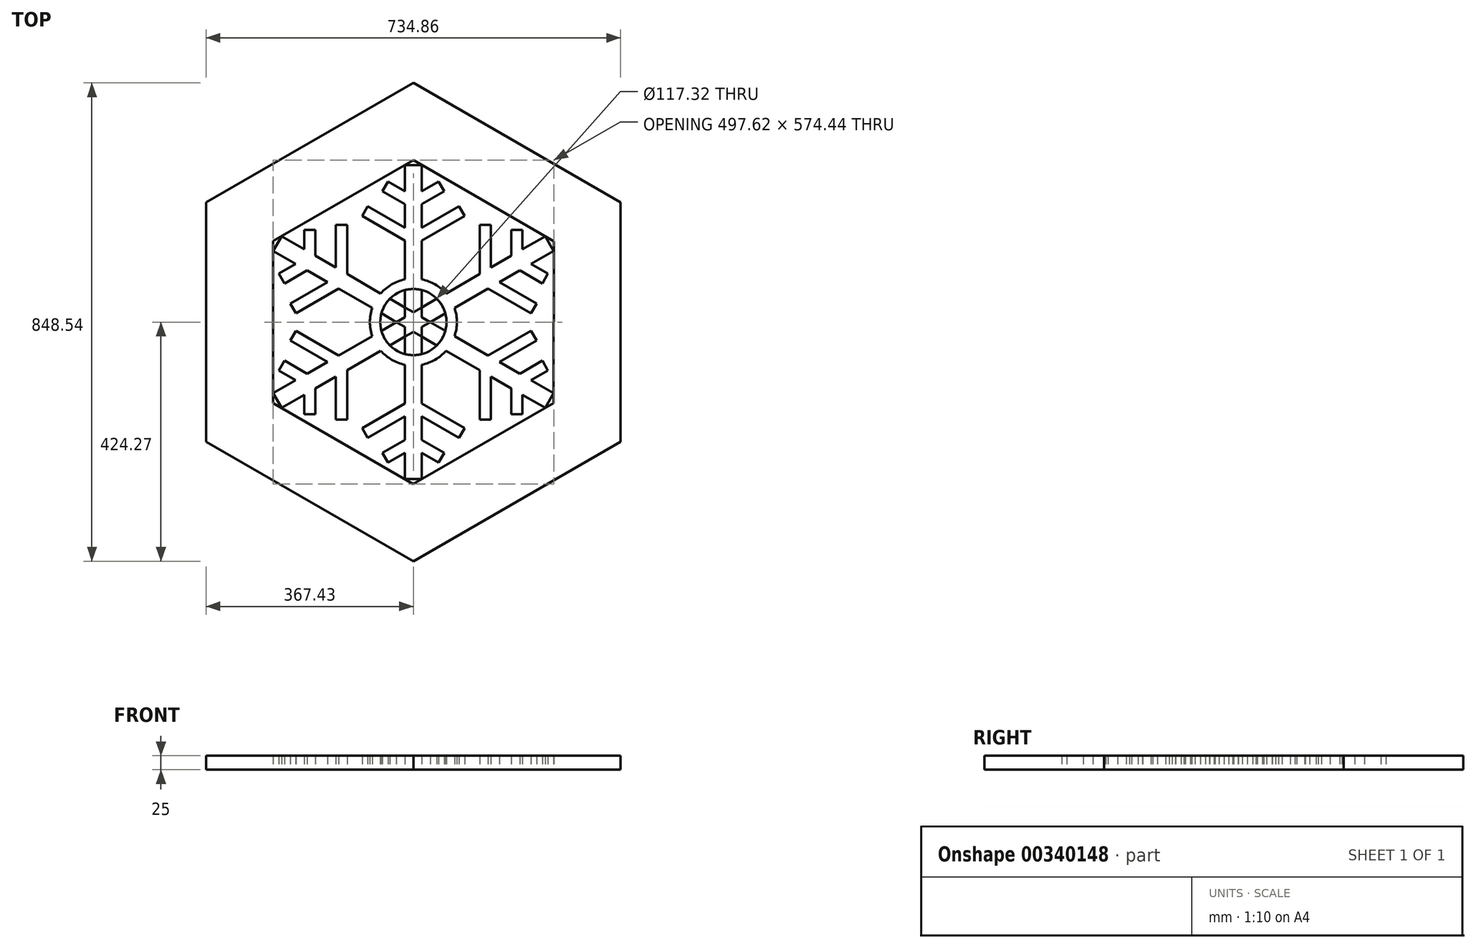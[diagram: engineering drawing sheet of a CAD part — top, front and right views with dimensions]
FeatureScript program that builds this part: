
annotation { "Feature Type Name" : "Feature", "Feature Type Description" : "" }
export const myFeature = defineFeature(function(context is Context, id is Id, definition is map)
    precondition{}
    {
        {
            var Q0;
            Q0=qCreatedBy(makeId("Top.planeOp"),FACE);
            var sketch = newSketch(context, id + "F0", { "sketchPlane" : qUnion([Q0])});
            skLineSegment(sketch, "E0", {"start": v(0, 439.87) * mm, "end": v(0, -254.88) * mm, "construction": true});
            skLineSegment(sketch, "E1", {"start": v(0, 278.5) * mm, "end": v(-15, 278.5) * mm});
            skLineSegment(sketch, "E2", {"start": v(-15, 278.5) * mm, "end": v(-15, 232.17) * mm});
            skLineSegment(sketch, "E3", {"start": v(-15, 232.17) * mm, "end": v(-45, 249.5) * mm});
            skLineSegment(sketch, "E4", {"start": v(-45, 249.5) * mm, "end": v(-55, 232.17) * mm});
            skLineSegment(sketch, "E5", {"start": v(-55, 232.17) * mm, "end": v(-15, 209.08) * mm});
            skLineSegment(sketch, "E6", {"start": v(-45, 249.5) * mm, "end": v(-55, 232.17) * mm, "construction": true});
            skLineSegment(sketch, "E7", {"start": v(-40.34, 275.63) * mm, "end": v(-118.1, 140.94) * mm, "construction": true});
            skLineSegment(sketch, "E8", {"start": v(-15, 209.08) * mm, "end": v(-15, 167.41) * mm});
            skLineSegment(sketch, "E9", {"start": v(-15, 167.41) * mm, "end": v(-80.86, 205.44) * mm});
            skLineSegment(sketch, "E10", {"start": v(-80.86, 205.44) * mm, "end": v(-90.86, 188.12) * mm});
            skLineSegment(sketch, "E11", {"start": v(-90.86, 188.12) * mm, "end": v(-15, 144.32) * mm});
            skLineSegment(sketch, "E12", {"start": v(-15, 144.32) * mm, "end": v(-15, 0) * mm});
            skLineSegment(sketch, "E13", {"start": v(-15, 0) * mm, "end": v(0, 0) * mm});
            skLineSegment(sketch, "E14.MirrorCS", {"start": v(0, 278.5) * mm, "end": v(15, 278.5) * mm});
            skLineSegment(sketch, "E15.MirrorCS", {"start": v(15, 278.5) * mm, "end": v(15, 232.17) * mm});
            skLineSegment(sketch, "E16.MirrorCS", {"start": v(15, 232.17) * mm, "end": v(45, 249.5) * mm});
            skLineSegment(sketch, "E17.MirrorCS", {"start": v(45, 249.5) * mm, "end": v(55, 232.17) * mm});
            skLineSegment(sketch, "E18.MirrorCS", {"start": v(55, 232.17) * mm, "end": v(15, 209.08) * mm});
            skLineSegment(sketch, "E19.MirrorCS", {"start": v(15, 167.41) * mm, "end": v(80.86, 205.44) * mm});
            skLineSegment(sketch, "E20.MirrorCS", {"start": v(15, 209.08) * mm, "end": v(15, 167.41) * mm});
            skLineSegment(sketch, "E21.MirrorCS", {"start": v(90.86, 188.12) * mm, "end": v(15, 144.32) * mm});
            skLineSegment(sketch, "E22.MirrorCS", {"start": v(80.86, 205.44) * mm, "end": v(90.86, 188.12) * mm});
            skLineSegment(sketch, "E23.MirrorCS", {"start": v(15, 144.32) * mm, "end": v(15, 0) * mm});
            skLineSegment(sketch, "E24.MirrorCS", {"start": v(15, 0) * mm, "end": v(0, 0) * mm});
            skLineSegment(sketch, "E25.1.0", {"start": v(-193.57, 129.08) * mm, "end": v(-193.57, 163.72) * mm});
            skLineSegment(sketch, "E25.1.1", {"start": v(-238.57, 85.77) * mm, "end": v(-228.57, 68.45) * mm, "construction": true});
            skLineSegment(sketch, "E25.1.2", {"start": v(-228.57, 68.45) * mm, "end": v(-188.57, 91.55) * mm});
            skLineSegment(sketch, "E25.1.3", {"start": v(-173.57, 163.72) * mm, "end": v(-173.57, 117.53) * mm});
            skLineSegment(sketch, "E25.1.4", {"start": v(-188.57, 91.55) * mm, "end": v(-152.49, 70.72) * mm});
            skLineSegment(sketch, "E25.1.5", {"start": v(-258.87, 102.88) * mm, "end": v(-181.1, -31.81) * mm, "construction": true});
            skLineSegment(sketch, "E25.1.6", {"start": v(-173.57, 117.53) * mm, "end": v(-137.49, 96.7) * mm});
            skLineSegment(sketch, "E25.1.7", {"start": v(-208.57, 103.1) * mm, "end": v(-238.57, 85.77) * mm});
            skLineSegment(sketch, "E25.1.8", {"start": v(-248.68, 126.26) * mm, "end": v(-208.57, 103.1) * mm});
            skLineSegment(sketch, "E25.1.9", {"start": v(-152.49, 70.72) * mm, "end": v(-218.35, 32.7) * mm});
            skLineSegment(sketch, "E25.1.10", {"start": v(-208.35, 15.37) * mm, "end": v(-132.49, 59.17) * mm});
            skLineSegment(sketch, "E25.1.11", {"start": v(-117.49, 85.15) * mm, "end": v(7.5, 13) * mm});
            skLineSegment(sketch, "E25.1.12", {"start": v(-137.49, 172.75) * mm, "end": v(-117.49, 172.75) * mm});
            skLineSegment(sketch, "E25.1.13", {"start": v(-117.49, 172.75) * mm, "end": v(-117.49, 85.15) * mm});
            skLineSegment(sketch, "E25.1.14", {"start": v(-132.49, 59.17) * mm, "end": v(-7.5, -13) * mm});
            skLineSegment(sketch, "E25.1.15", {"start": v(-137.49, 96.7) * mm, "end": v(-137.49, 172.75) * mm});
            skLineSegment(sketch, "E25.1.16", {"start": v(-233.68, 152.24) * mm, "end": v(-193.57, 129.08) * mm});
            skLineSegment(sketch, "E25.1.17", {"start": v(-193.57, 163.72) * mm, "end": v(-173.57, 163.72) * mm});
            skLineSegment(sketch, "E25.1.18", {"start": v(-238.57, 85.77) * mm, "end": v(-228.57, 68.45) * mm});
            skLineSegment(sketch, "E25.1.19", {"start": v(-218.35, 32.7) * mm, "end": v(-208.35, 15.37) * mm});
            skLineSegment(sketch, "E25.1.20", {"start": v(-241.18, 139.25) * mm, "end": v(-233.68, 152.24) * mm});
            skLineSegment(sketch, "E25.1.21", {"start": v(7.5, 13) * mm, "end": v(0, 0) * mm});
            skLineSegment(sketch, "E25.1.22", {"start": v(-7.5, -13) * mm, "end": v(0, 0) * mm});
            skLineSegment(sketch, "E25.1.23", {"start": v(-241.18, 139.25) * mm, "end": v(-248.68, 126.26) * mm});
            skLineSegment(sketch, "E25.2.0", {"start": v(-208.57, -103.1) * mm, "end": v(-238.57, -85.77) * mm});
            skLineSegment(sketch, "E25.2.1", {"start": v(-193.57, -163.72) * mm, "end": v(-173.57, -163.72) * mm, "construction": true});
            skLineSegment(sketch, "E25.2.2", {"start": v(-173.57, -163.72) * mm, "end": v(-173.57, -117.53) * mm});
            skLineSegment(sketch, "E25.2.3", {"start": v(-228.57, -68.45) * mm, "end": v(-188.57, -91.55) * mm});
            skLineSegment(sketch, "E25.2.4", {"start": v(-173.57, -117.53) * mm, "end": v(-137.49, -96.7) * mm});
            skLineSegment(sketch, "E25.2.5", {"start": v(-218.53, -172.75) * mm, "end": v(-63, -172.75) * mm, "construction": true});
            skLineSegment(sketch, "E25.2.6", {"start": v(-188.57, -91.55) * mm, "end": v(-152.49, -70.72) * mm});
            skLineSegment(sketch, "E25.2.7", {"start": v(-193.57, -129.08) * mm, "end": v(-193.57, -163.72) * mm});
            skLineSegment(sketch, "E25.2.8", {"start": v(-233.68, -152.24) * mm, "end": v(-193.57, -129.08) * mm});
            skLineSegment(sketch, "E25.2.9", {"start": v(-137.49, -96.7) * mm, "end": v(-137.49, -172.75) * mm});
            skLineSegment(sketch, "E25.2.10", {"start": v(-117.49, -172.75) * mm, "end": v(-117.49, -85.15) * mm});
            skLineSegment(sketch, "E25.2.11", {"start": v(-132.49, -59.17) * mm, "end": v(-7.5, 13) * mm});
            skLineSegment(sketch, "E25.2.12", {"start": v(-218.35, -32.7) * mm, "end": v(-208.35, -15.37) * mm});
            skLineSegment(sketch, "E25.2.13", {"start": v(-208.35, -15.37) * mm, "end": v(-132.49, -59.17) * mm});
            skLineSegment(sketch, "E25.2.14", {"start": v(-117.49, -85.15) * mm, "end": v(7.5, -13) * mm});
            skLineSegment(sketch, "E25.2.15", {"start": v(-152.49, -70.72) * mm, "end": v(-218.35, -32.7) * mm});
            skLineSegment(sketch, "E25.2.16", {"start": v(-248.68, -126.26) * mm, "end": v(-208.57, -103.1) * mm});
            skLineSegment(sketch, "E25.2.17", {"start": v(-238.57, -85.77) * mm, "end": v(-228.57, -68.45) * mm});
            skLineSegment(sketch, "E25.2.18", {"start": v(-193.57, -163.72) * mm, "end": v(-173.57, -163.72) * mm});
            skLineSegment(sketch, "E25.2.19", {"start": v(-137.49, -172.75) * mm, "end": v(-117.49, -172.75) * mm});
            skLineSegment(sketch, "E25.2.20", {"start": v(-241.18, -139.25) * mm, "end": v(-248.68, -126.26) * mm});
            skLineSegment(sketch, "E25.2.21", {"start": v(-7.5, 13) * mm, "end": v(0, 0) * mm});
            skLineSegment(sketch, "E25.2.22", {"start": v(7.5, -13) * mm, "end": v(0, 0) * mm});
            skLineSegment(sketch, "E25.2.23", {"start": v(-241.18, -139.25) * mm, "end": v(-233.68, -152.24) * mm});
            skLineSegment(sketch, "E25.3.0", {"start": v(-15, -232.17) * mm, "end": v(-45, -249.5) * mm});
            skLineSegment(sketch, "E25.3.1", {"start": v(45, -249.5) * mm, "end": v(55, -232.17) * mm, "construction": true});
            skLineSegment(sketch, "E25.3.2", {"start": v(55, -232.17) * mm, "end": v(15, -209.08) * mm});
            skLineSegment(sketch, "E25.3.3", {"start": v(-55, -232.17) * mm, "end": v(-15, -209.08) * mm});
            skLineSegment(sketch, "E25.3.4", {"start": v(15, -209.08) * mm, "end": v(15, -167.41) * mm});
            skLineSegment(sketch, "E25.3.5", {"start": v(40.34, -275.63) * mm, "end": v(118.1, -140.94) * mm, "construction": true});
            skLineSegment(sketch, "E25.3.6", {"start": v(-15, -209.08) * mm, "end": v(-15, -167.41) * mm});
            skLineSegment(sketch, "E25.3.7", {"start": v(15, -232.17) * mm, "end": v(45, -249.5) * mm});
            skLineSegment(sketch, "E25.3.8", {"start": v(15, -278.5) * mm, "end": v(15, -232.17) * mm});
            skLineSegment(sketch, "E25.3.9", {"start": v(15, -167.41) * mm, "end": v(80.86, -205.44) * mm});
            skLineSegment(sketch, "E25.3.10", {"start": v(90.86, -188.12) * mm, "end": v(15, -144.32) * mm});
            skLineSegment(sketch, "E25.3.11", {"start": v(-15, -144.32) * mm, "end": v(-15, 0) * mm});
            skLineSegment(sketch, "E25.3.12", {"start": v(-80.86, -205.44) * mm, "end": v(-90.86, -188.12) * mm});
            skLineSegment(sketch, "E25.3.13", {"start": v(-90.86, -188.12) * mm, "end": v(-15, -144.32) * mm});
            skLineSegment(sketch, "E25.3.14", {"start": v(15, -144.32) * mm, "end": v(15, 0) * mm});
            skLineSegment(sketch, "E25.3.15", {"start": v(-15, -167.41) * mm, "end": v(-80.86, -205.44) * mm});
            skLineSegment(sketch, "E25.3.16", {"start": v(-15, -278.5) * mm, "end": v(-15, -232.17) * mm});
            skLineSegment(sketch, "E25.3.17", {"start": v(-45, -249.5) * mm, "end": v(-55, -232.17) * mm});
            skLineSegment(sketch, "E25.3.18", {"start": v(45, -249.5) * mm, "end": v(55, -232.17) * mm});
            skLineSegment(sketch, "E25.3.19", {"start": v(80.86, -205.44) * mm, "end": v(90.86, -188.12) * mm});
            skLineSegment(sketch, "E25.3.20", {"start": v(0, -278.5) * mm, "end": v(-15, -278.5) * mm});
            skLineSegment(sketch, "E25.3.23", {"start": v(0, -278.5) * mm, "end": v(15, -278.5) * mm});
            skLineSegment(sketch, "E25.4.0", {"start": v(193.57, -129.08) * mm, "end": v(193.57, -163.72) * mm});
            skLineSegment(sketch, "E25.4.1", {"start": v(238.57, -85.77) * mm, "end": v(228.57, -68.45) * mm, "construction": true});
            skLineSegment(sketch, "E25.4.2", {"start": v(228.57, -68.45) * mm, "end": v(188.57, -91.55) * mm});
            skLineSegment(sketch, "E25.4.3", {"start": v(173.57, -163.72) * mm, "end": v(173.57, -117.53) * mm});
            skLineSegment(sketch, "E25.4.4", {"start": v(188.57, -91.55) * mm, "end": v(152.49, -70.72) * mm});
            skLineSegment(sketch, "E25.4.5", {"start": v(258.87, -102.88) * mm, "end": v(181.1, 31.81) * mm, "construction": true});
            skLineSegment(sketch, "E25.4.6", {"start": v(173.57, -117.53) * mm, "end": v(137.49, -96.7) * mm});
            skLineSegment(sketch, "E25.4.7", {"start": v(208.57, -103.1) * mm, "end": v(238.57, -85.77) * mm});
            skLineSegment(sketch, "E25.4.8", {"start": v(248.68, -126.26) * mm, "end": v(208.57, -103.1) * mm});
            skLineSegment(sketch, "E25.4.9", {"start": v(152.49, -70.72) * mm, "end": v(218.35, -32.7) * mm});
            skLineSegment(sketch, "E25.4.10", {"start": v(208.35, -15.37) * mm, "end": v(132.49, -59.17) * mm});
            skLineSegment(sketch, "E25.4.11", {"start": v(117.49, -85.15) * mm, "end": v(-7.5, -13) * mm});
            skLineSegment(sketch, "E25.4.12", {"start": v(137.49, -172.75) * mm, "end": v(117.49, -172.75) * mm});
            skLineSegment(sketch, "E25.4.13", {"start": v(117.49, -172.75) * mm, "end": v(117.49, -85.15) * mm});
            skLineSegment(sketch, "E25.4.14", {"start": v(132.49, -59.17) * mm, "end": v(7.5, 13) * mm});
            skLineSegment(sketch, "E25.4.15", {"start": v(137.49, -96.7) * mm, "end": v(137.49, -172.75) * mm});
            skLineSegment(sketch, "E25.4.16", {"start": v(233.68, -152.24) * mm, "end": v(193.57, -129.08) * mm});
            skLineSegment(sketch, "E25.4.17", {"start": v(193.57, -163.72) * mm, "end": v(173.57, -163.72) * mm});
            skLineSegment(sketch, "E25.4.18", {"start": v(238.57, -85.77) * mm, "end": v(228.57, -68.45) * mm});
            skLineSegment(sketch, "E25.4.19", {"start": v(218.35, -32.7) * mm, "end": v(208.35, -15.37) * mm});
            skLineSegment(sketch, "E25.4.20", {"start": v(241.18, -139.25) * mm, "end": v(233.68, -152.24) * mm});
            skLineSegment(sketch, "E25.4.21", {"start": v(-7.5, -13) * mm, "end": v(0, 0) * mm});
            skLineSegment(sketch, "E25.4.22", {"start": v(7.5, 13) * mm, "end": v(0, 0) * mm});
            skLineSegment(sketch, "E25.4.23", {"start": v(241.18, -139.25) * mm, "end": v(248.68, -126.26) * mm});
            skLineSegment(sketch, "E25.5.0", {"start": v(208.57, 103.1) * mm, "end": v(238.57, 85.77) * mm});
            skLineSegment(sketch, "E25.5.1", {"start": v(193.57, 163.72) * mm, "end": v(173.57, 163.72) * mm, "construction": true});
            skLineSegment(sketch, "E25.5.2", {"start": v(173.57, 163.72) * mm, "end": v(173.57, 117.53) * mm});
            skLineSegment(sketch, "E25.5.3", {"start": v(228.57, 68.45) * mm, "end": v(188.57, 91.55) * mm});
            skLineSegment(sketch, "E25.5.4", {"start": v(173.57, 117.53) * mm, "end": v(137.49, 96.7) * mm});
            skLineSegment(sketch, "E25.5.5", {"start": v(218.53, 172.75) * mm, "end": v(63, 172.75) * mm, "construction": true});
            skLineSegment(sketch, "E25.5.6", {"start": v(188.57, 91.55) * mm, "end": v(152.49, 70.72) * mm});
            skLineSegment(sketch, "E25.5.7", {"start": v(193.57, 129.08) * mm, "end": v(193.57, 163.72) * mm});
            skLineSegment(sketch, "E25.5.8", {"start": v(233.68, 152.24) * mm, "end": v(193.57, 129.08) * mm});
            skLineSegment(sketch, "E25.5.9", {"start": v(137.49, 96.7) * mm, "end": v(137.49, 172.75) * mm});
            skLineSegment(sketch, "E25.5.10", {"start": v(117.49, 172.75) * mm, "end": v(117.49, 85.15) * mm});
            skLineSegment(sketch, "E25.5.11", {"start": v(132.49, 59.17) * mm, "end": v(7.5, -13) * mm});
            skLineSegment(sketch, "E25.5.12", {"start": v(218.35, 32.7) * mm, "end": v(208.35, 15.37) * mm});
            skLineSegment(sketch, "E25.5.13", {"start": v(208.35, 15.37) * mm, "end": v(132.49, 59.17) * mm});
            skLineSegment(sketch, "E25.5.14", {"start": v(117.49, 85.15) * mm, "end": v(-7.5, 13) * mm});
            skLineSegment(sketch, "E25.5.15", {"start": v(152.49, 70.72) * mm, "end": v(218.35, 32.7) * mm});
            skLineSegment(sketch, "E25.5.16", {"start": v(248.68, 126.26) * mm, "end": v(208.57, 103.1) * mm});
            skLineSegment(sketch, "E25.5.17", {"start": v(238.57, 85.77) * mm, "end": v(228.57, 68.45) * mm});
            skLineSegment(sketch, "E25.5.18", {"start": v(193.57, 163.72) * mm, "end": v(173.57, 163.72) * mm});
            skLineSegment(sketch, "E25.5.19", {"start": v(137.49, 172.75) * mm, "end": v(117.49, 172.75) * mm});
            skLineSegment(sketch, "E25.5.20", {"start": v(241.18, 139.25) * mm, "end": v(248.68, 126.26) * mm});
            skLineSegment(sketch, "E25.5.21", {"start": v(7.5, -13) * mm, "end": v(0, 0) * mm});
            skLineSegment(sketch, "E25.5.22", {"start": v(-7.5, 13) * mm, "end": v(0, 0) * mm});
            skLineSegment(sketch, "E25.5.23", {"start": v(241.18, 139.25) * mm, "end": v(233.68, 152.24) * mm});
            skPoint(sketch, "E25.center", {"position": v(0, 0) * mm});
            skCircle(sketch, "E26", {"center": v(0, 0) * mm, "radius": 77.12 * mm});
            skCircle(sketch, "E27", {"center": v(0, 0) * mm, "radius": 58.66 * mm});
            skCircle(sketch, "E28.cCircle", {"center": v(0, 0) * mm, "radius": 367.43 * mm, "construction": true});
            skLineSegment(sketch, "E28.0", {"start": v(367.43, -212.14) * mm, "end": v(0, -424.27) * mm});
            skLineSegment(sketch, "E28.1", {"start": v(0, -424.27) * mm, "end": v(-367.43, -212.14) * mm});
            skLineSegment(sketch, "E28.2", {"start": v(-367.43, -212.14) * mm, "end": v(-367.43, 212.14) * mm});
            skLineSegment(sketch, "E28.3", {"start": v(-367.43, 212.14) * mm, "end": v(0, 424.27) * mm});
            skLineSegment(sketch, "E28.4", {"start": v(0, 424.27) * mm, "end": v(367.43, 212.14) * mm});
            skLineSegment(sketch, "E28.5", {"start": v(367.43, 212.14) * mm, "end": v(367.43, -212.14) * mm});
            skPoint(sketch, "E28.0.midPoint", {"position": v(183.72, -318.2) * mm});
            skCircle(sketch, "E29.cCircle", {"center": v(0, 0) * mm, "radius": 248.74 * mm, "construction": true});
            skLineSegment(sketch, "E29.0", {"start": v(-248.67, 143.73) * mm, "end": v(0.14, 287.22) * mm});
            skLineSegment(sketch, "E29.1", {"start": v(0.14, 287.22) * mm, "end": v(248.8, 143.5) * mm});
            skLineSegment(sketch, "E29.2", {"start": v(248.8, 143.5) * mm, "end": v(248.67, -143.73) * mm});
            skLineSegment(sketch, "E29.3", {"start": v(248.67, -143.73) * mm, "end": v(-0.14, -287.22) * mm});
            skLineSegment(sketch, "E29.4", {"start": v(-0.14, -287.22) * mm, "end": v(-248.8, -143.5) * mm});
            skLineSegment(sketch, "E29.5", {"start": v(-248.8, -143.5) * mm, "end": v(-248.67, 143.73) * mm});
            skPoint(sketch, "E29.0.midPoint", {"position": v(-124.27, 215.48) * mm});
            skSolve(sketch);
        }
        {
            var Q0;
            Q0=makeQuery(id+"F0.imprint","IMPRINT",FACE,{"disambiguationData":[TD([[makeQuery(id+"F0.imprint","IMPRINT",EDGE,{"derivedFrom":sQuery(id+"F0.wireOp",EDGE,"E28.0")}),-1.0]])]});
            var Q1;
            Q1=makeQuery(id+"F0.imprint","IMPRINT",FACE,{"disambiguationData":[TD([[makeQuery(id+"F0.imprint","IMPRINT",EDGE,{"derivedFrom":sQuery(id+"F0.wireOp",EDGE,"E25.1.0")}),-1.0]])]});
            var Q2;
            Q2=makeQuery(id+"F0.imprint","IMPRINT",FACE,{"disambiguationData":[TD([[makeQuery(id+"F0.imprint","IMPRINT",EDGE,{"derivedFrom":sQuery(id+"F0.wireOp",EDGE,"E1")}),1.0]])]});
            var Q3;
            Q3=makeQuery(id+"F0.imprint","IMPRINT",FACE,{"disambiguationData":[TD([[makeQuery(id+"F0.imprint","IMPRINT",EDGE,{"derivedFrom":sQuery(id+"F0.wireOp",EDGE,"E25.5.0")}),-1.0]])]});
            var Q4;
            Q4=makeQuery(id+"F0.imprint","IMPRINT",FACE,{"disambiguationData":[TD([[makeQuery(id+"F0.imprint","IMPRINT",EDGE,{"derivedFrom":sQuery(id+"F0.wireOp",EDGE,"E25.4.0")}),-1.0]])]});
            var Q5;
            Q5=makeQuery(id+"F0.imprint","IMPRINT",FACE,{"disambiguationData":[TD([[makeQuery(id+"F0.imprint","IMPRINT",EDGE,{"derivedFrom":sQuery(id+"F0.wireOp",EDGE,"E25.3.0")}),-1.0]])]});
            var Q6;
            Q6=makeQuery(id+"F0.imprint","IMPRINT",FACE,{"disambiguationData":[TD([[makeQuery(id+"F0.imprint","IMPRINT",EDGE,{"derivedFrom":sQuery(id+"F0.wireOp",EDGE,"E25.2.0")}),-1.0]])]});
            var Q7;
            {var subQ0=sQuery(id+"F0.wireOp",EDGE,"E26");var subQ1=sQuery(id+"F0.wireOp",EDGE,"E25.1.14");var subQ2=makeQuery(id+"F0.imprint","INTERSECT",VERTEX,{"derivedFrom":[subQ1,subQ0]});Q7=makeQuery(id+"F0.imprint","IMPRINT",FACE,{"disambiguationData":[TD([[makeQuery(id+"F0.imprint","IMPRINT",EDGE,{"disambiguationData":[TD([[subQ2,-1.0]])],"derivedFrom":subQ1}),-1.0]])]});}
            var Q8;
            {var subQ0=sQuery(id+"F0.wireOp",EDGE,"E26");var subQ1=sQuery(id+"F0.wireOp",EDGE,"E25.1.11");var subQ2=makeQuery(id+"F0.imprint","INTERSECT",VERTEX,{"derivedFrom":[subQ1,subQ0]});Q8=makeQuery(id+"F0.imprint","IMPRINT",FACE,{"disambiguationData":[TD([[makeQuery(id+"F0.imprint","IMPRINT",EDGE,{"disambiguationData":[TD([[subQ2,-1.0]])],"derivedFrom":subQ1}),-1.0]])]});}
            var Q9;
            {var subQ0=sQuery(id+"F0.wireOp",EDGE,"E26");var subQ1=sQuery(id+"F0.wireOp",EDGE,"E12");var subQ2=makeQuery(id+"F0.imprint","INTERSECT",VERTEX,{"derivedFrom":[subQ1,subQ0]});Q9=makeQuery(id+"F0.imprint","IMPRINT",FACE,{"disambiguationData":[TD([[makeQuery(id+"F0.imprint","IMPRINT",EDGE,{"disambiguationData":[TD([[subQ2,-1.0]])],"derivedFrom":subQ1}),-1.0]])]});}
            var Q10;
            {var subQ0=sQuery(id+"F0.wireOp",EDGE,"E26");var subQ1=sQuery(id+"F0.wireOp",EDGE,"E12");var subQ2=makeQuery(id+"F0.imprint","INTERSECT",VERTEX,{"derivedFrom":[subQ1,subQ0]});Q10=makeQuery(id+"F0.imprint","IMPRINT",FACE,{"disambiguationData":[TD([[makeQuery(id+"F0.imprint","IMPRINT",EDGE,{"disambiguationData":[TD([[subQ2,-1.0]])],"derivedFrom":subQ1}),1.0]])]});}
            var Q11;
            {var subQ0=sQuery(id+"F0.wireOp",EDGE,"E26");var subQ1=sQuery(id+"F0.wireOp",EDGE,"E23.MirrorCS");var subQ2=makeQuery(id+"F0.imprint","INTERSECT",VERTEX,{"derivedFrom":[subQ1,subQ0]});Q11=makeQuery(id+"F0.imprint","IMPRINT",FACE,{"disambiguationData":[TD([[makeQuery(id+"F0.imprint","IMPRINT",EDGE,{"disambiguationData":[TD([[subQ2,-1.0]])],"derivedFrom":subQ1}),1.0]])]});}
            var Q12;
            {var subQ0=sQuery(id+"F0.wireOp",EDGE,"E26");var subQ1=sQuery(id+"F0.wireOp",EDGE,"E25.5.11");var subQ2=makeQuery(id+"F0.imprint","INTERSECT",VERTEX,{"derivedFrom":[subQ1,subQ0]});Q12=makeQuery(id+"F0.imprint","IMPRINT",FACE,{"disambiguationData":[TD([[makeQuery(id+"F0.imprint","IMPRINT",EDGE,{"disambiguationData":[TD([[subQ2,-1.0]])],"derivedFrom":subQ1}),-1.0]])]});}
            var Q13;
            {var subQ0=sQuery(id+"F0.wireOp",EDGE,"E26");var subQ1=sQuery(id+"F0.wireOp",EDGE,"E25.4.14");var subQ2=makeQuery(id+"F0.imprint","INTERSECT",VERTEX,{"derivedFrom":[subQ1,subQ0]});Q13=makeQuery(id+"F0.imprint","IMPRINT",FACE,{"disambiguationData":[TD([[makeQuery(id+"F0.imprint","IMPRINT",EDGE,{"disambiguationData":[TD([[subQ2,-1.0]])],"derivedFrom":subQ1}),-1.0]])]});}
            var Q14;
            {var subQ0=sQuery(id+"F0.wireOp",EDGE,"E26");var subQ1=sQuery(id+"F0.wireOp",EDGE,"E25.4.11");var subQ2=makeQuery(id+"F0.imprint","INTERSECT",VERTEX,{"derivedFrom":[subQ1,subQ0]});Q14=makeQuery(id+"F0.imprint","IMPRINT",FACE,{"disambiguationData":[TD([[makeQuery(id+"F0.imprint","IMPRINT",EDGE,{"disambiguationData":[TD([[subQ2,-1.0]])],"derivedFrom":subQ1}),-1.0]])]});}
            var Q15;
            {var subQ0=sQuery(id+"F0.wireOp",EDGE,"E26");var subQ1=sQuery(id+"F0.wireOp",EDGE,"E25.3.14");var subQ2=makeQuery(id+"F0.imprint","INTERSECT",VERTEX,{"derivedFrom":[subQ1,subQ0]});Q15=makeQuery(id+"F0.imprint","IMPRINT",FACE,{"disambiguationData":[TD([[makeQuery(id+"F0.imprint","IMPRINT",EDGE,{"disambiguationData":[TD([[subQ2,-1.0]])],"derivedFrom":subQ1}),-1.0]])]});}
            var Q16;
            {var subQ0=sQuery(id+"F0.wireOp",EDGE,"E26");var subQ1=sQuery(id+"F0.wireOp",EDGE,"E25.3.11");var subQ2=makeQuery(id+"F0.imprint","INTERSECT",VERTEX,{"derivedFrom":[subQ1,subQ0]});Q16=makeQuery(id+"F0.imprint","IMPRINT",FACE,{"disambiguationData":[TD([[makeQuery(id+"F0.imprint","IMPRINT",EDGE,{"disambiguationData":[TD([[subQ2,-1.0]])],"derivedFrom":subQ1}),-1.0]])]});}
            var Q17;
            {var subQ0=sQuery(id+"F0.wireOp",EDGE,"E26");var subQ1=sQuery(id+"F0.wireOp",EDGE,"E25.2.14");var subQ2=makeQuery(id+"F0.imprint","INTERSECT",VERTEX,{"derivedFrom":[subQ1,subQ0]});Q17=makeQuery(id+"F0.imprint","IMPRINT",FACE,{"disambiguationData":[TD([[makeQuery(id+"F0.imprint","IMPRINT",EDGE,{"disambiguationData":[TD([[subQ2,-1.0]])],"derivedFrom":subQ1}),-1.0]])]});}
            var Q18;
            {var subQ0=sQuery(id+"F0.wireOp",EDGE,"E26");var subQ1=sQuery(id+"F0.wireOp",EDGE,"E25.2.11");var subQ2=makeQuery(id+"F0.imprint","INTERSECT",VERTEX,{"derivedFrom":[subQ1,subQ0]});Q18=makeQuery(id+"F0.imprint","IMPRINT",FACE,{"disambiguationData":[TD([[makeQuery(id+"F0.imprint","IMPRINT",EDGE,{"disambiguationData":[TD([[subQ2,-1.0]])],"derivedFrom":subQ1}),-1.0]])]});}
            extrude(context, id + "F1", {"entities" : qUnion([Q0, Q1, Q2, Q3, Q4, Q5, Q6, Q7, Q8, Q9, Q10, Q11, Q12, Q13, Q14, Q15, Q16, Q17, Q18]), "depth" : 25 * mm});
        }
        {
            var Q0;
            {var subQ1=sQuery(id+"F0.wireOp",EDGE,"E12");var subQ7=sQuery(id+"F0.wireOp",EDGE,"E25.1.11");var subQ8=makeQuery(id+"F0.imprint","INTERSECT",VERTEX,{"derivedFrom":[subQ1,subQ7]});Q0=makeQuery(id+"F0.imprint","IMPRINT",FACE,{"disambiguationData":[TD([[makeQuery(id+"F0.imprint","IMPRINT",EDGE,{"disambiguationData":[TD([[subQ8,-1.0]])],"derivedFrom":subQ1}),-1.0]])]});}
            var Q1;
            {var subQ5=sQuery(id+"F0.wireOp",EDGE,"E12");var subQ7=sQuery(id+"F0.wireOp",EDGE,"E27");var subQ9=makeQuery(id+"F0.imprint","INTERSECT",VERTEX,{"derivedFrom":[subQ5,subQ7]});Q1=makeQuery(id+"F0.imprint","IMPRINT",FACE,{"disambiguationData":[TD([[makeQuery(id+"F0.imprint","IMPRINT",EDGE,{"disambiguationData":[TD([[subQ9,-1.0]])],"derivedFrom":subQ5}),1.0]])]});}
            var Q2;
            {var subQ0=sQuery(id+"F0.wireOp",EDGE,"E25.5.14");var subQ1=sQuery(id+"F0.wireOp",EDGE,"E23.MirrorCS");var subQ2=makeQuery(id+"F0.imprint","INTERSECT",VERTEX,{"derivedFrom":[subQ1,subQ0]});Q2=makeQuery(id+"F0.imprint","IMPRINT",FACE,{"disambiguationData":[TD([[makeQuery(id+"F0.imprint","IMPRINT",EDGE,{"disambiguationData":[TD([[subQ2,-1.0]])],"derivedFrom":subQ1}),1.0]])]});}
            var Q3;
            {var subQ1=sQuery(id+"F0.wireOp",EDGE,"E25.3.14");var subQ7=sQuery(id+"F0.wireOp",EDGE,"E25.4.11");var subQ8=makeQuery(id+"F0.imprint","INTERSECT",VERTEX,{"derivedFrom":[subQ1,subQ7]});Q3=makeQuery(id+"F0.imprint","IMPRINT",FACE,{"disambiguationData":[TD([[makeQuery(id+"F0.imprint","IMPRINT",EDGE,{"disambiguationData":[TD([[subQ8,-1.0]])],"derivedFrom":subQ1}),-1.0]])]});}
            var Q4;
            {var subQ1=sQuery(id+"F0.wireOp",EDGE,"E25.2.14");var subQ7=sQuery(id+"F0.wireOp",EDGE,"E25.3.11");var subQ8=makeQuery(id+"F0.imprint","INTERSECT",VERTEX,{"derivedFrom":[subQ1,subQ7]});Q4=makeQuery(id+"F0.imprint","IMPRINT",FACE,{"disambiguationData":[TD([[makeQuery(id+"F0.imprint","IMPRINT",EDGE,{"disambiguationData":[TD([[subQ8,-1.0]])],"derivedFrom":subQ1}),-1.0]])]});}
            var Q5;
            {var subQ1=sQuery(id+"F0.wireOp",EDGE,"E25.1.14");var subQ7=sQuery(id+"F0.wireOp",EDGE,"E25.2.11");var subQ8=makeQuery(id+"F0.imprint","INTERSECT",VERTEX,{"derivedFrom":[subQ1,subQ7]});Q5=makeQuery(id+"F0.imprint","IMPRINT",FACE,{"disambiguationData":[TD([[makeQuery(id+"F0.imprint","IMPRINT",EDGE,{"disambiguationData":[TD([[subQ8,-1.0]])],"derivedFrom":subQ1}),-1.0]])]});}
            extrude(context, id + "F2", {"entities" : qUnion([Q0, Q1, Q2, Q3, Q4, Q5]), "depth" : 25 * mm});
        }
    });
